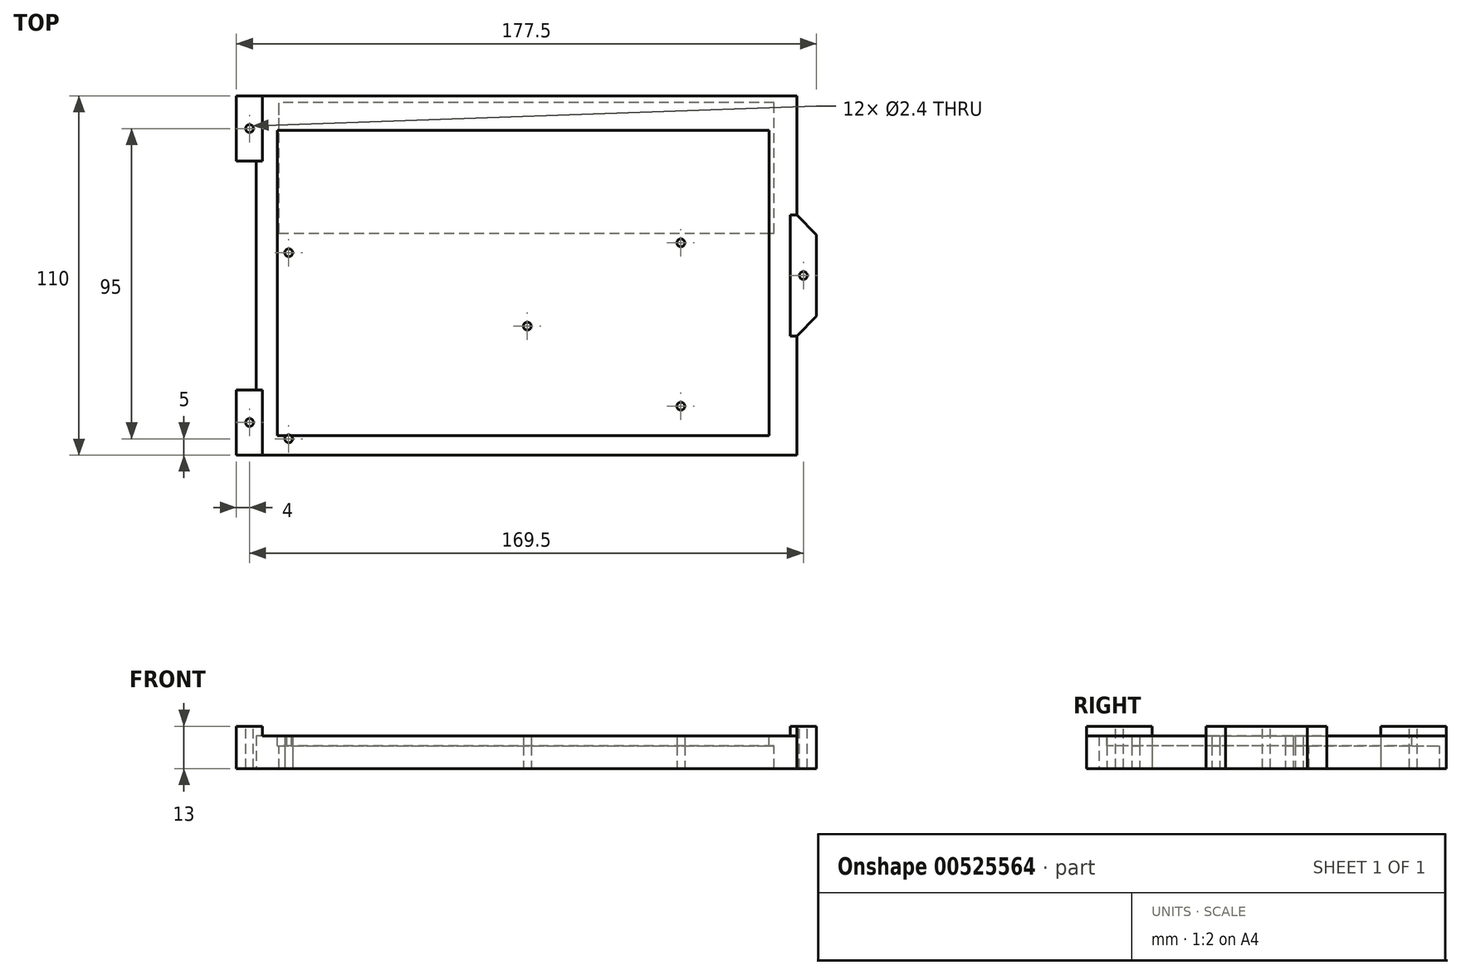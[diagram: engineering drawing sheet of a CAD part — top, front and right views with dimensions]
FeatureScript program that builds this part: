
annotation { "Feature Type Name" : "Feature", "Feature Type Description" : "" }
export const myFeature = defineFeature(function(context is Context, id is Id, definition is map)
    precondition{}
    {
        {
            var Q0;
            Q0=qCreatedBy(makeId("Top.planeOp"),FACE);
            var sketch = newSketch(context, id + "F0", { "sketchPlane" : qUnion([Q0])});
            skLineSegment(sketch, "E0.bottom", {"start": v(80.75, -53) * mm, "end": v(-80.75, -53) * mm});
            skLineSegment(sketch, "E0.top", {"start": v(80.75, 53) * mm, "end": v(-80.75, 53) * mm});
            skLineSegment(sketch, "E0.left", {"start": v(80.75, -53) * mm, "end": v(80.75, 53) * mm});
            skLineSegment(sketch, "E0.right", {"start": v(-80.75, -53) * mm, "end": v(-80.75, 53) * mm});
            skPoint(sketch, "E0.middle", {"position": v(0, 0) * mm});
            skLineSegment(sketch, "E1.bottom", {"start": v(82.75, -55) * mm, "end": v(-82.75, -55) * mm});
            skLineSegment(sketch, "E1.top", {"start": v(82.75, 55) * mm, "end": v(-82.75, 55) * mm});
            skLineSegment(sketch, "E1.left", {"start": v(82.75, -55) * mm, "end": v(82.75, 55) * mm});
            skLineSegment(sketch, "E1.right", {"start": v(-82.75, -55) * mm, "end": v(-82.75, 55) * mm});
            skLineSegment(sketch, "E2.bottom", {"start": v(-82.75, 55) * mm, "end": v(-88.75, 55) * mm});
            skLineSegment(sketch, "E2.top", {"start": v(-82.75, 35) * mm, "end": v(-88.75, 35) * mm});
            skLineSegment(sketch, "E2.left", {"start": v(-82.75, 55) * mm, "end": v(-82.75, 35) * mm});
            skLineSegment(sketch, "E2.right", {"start": v(-88.75, 55) * mm, "end": v(-88.75, 35) * mm});
            skLineSegment(sketch, "E3.bottom", {"start": v(-82.75, -55) * mm, "end": v(-88.75, -55) * mm});
            skLineSegment(sketch, "E3.top", {"start": v(-82.75, -35) * mm, "end": v(-88.75, -35) * mm});
            skLineSegment(sketch, "E3.left", {"start": v(-82.75, -55) * mm, "end": v(-82.75, -35) * mm});
            skLineSegment(sketch, "E3.right", {"start": v(-88.75, -55) * mm, "end": v(-88.75, -35) * mm});
            skLineSegment(sketch, "E4", {"start": v(88.75, 12.5) * mm, "end": v(88.75, -12.5) * mm});
            skLineSegment(sketch, "E5", {"start": v(88.75, -12.5) * mm, "end": v(82.75, -18.5) * mm});
            skLineSegment(sketch, "E6", {"start": v(88.75, 12.5) * mm, "end": v(82.75, 18.5) * mm});
            skSolve(sketch);
        }
        {
            var Q0;
            Q0 = qSketchRegion(id + "F0", true);
            extrude(context, id + "F1", {"entities" : qUnion([Q0]), "depth" : 10 * mm, "offsetDistance" : 25 * mm});
        }
        {
            var Q0;
            Q0=makeQuery(id+"F1.opExtrude","CAP_FACE",FACE,{"disambiguationData":[OSD([sQuery(id+"F0.wireOp",EDGE,"E0.bottom"),sQuery(id+"F0.wireOp",EDGE,"E0.top"),sQuery(id+"F0.wireOp",EDGE,"E0.left"),sQuery(id+"F0.wireOp",EDGE,"E0.right"),sQuery(id+"F0.wireOp",EDGE,"E1.bottom"),sQuery(id+"F0.wireOp",EDGE,"E1.top"),sQuery(id+"F0.wireOp",EDGE,"E1.left"),sQuery(id+"F0.wireOp",EDGE,"E1.right")])],"isStart":true});
            var sketch = newSketch(context, id + "F2", { "sketchPlane" : qUnion([Q0])});
            skLineSegment(sketch, "E7.bottom", {"start": v(-80.75, -53) * mm, "end": v(80.75, -53) * mm});
            skLineSegment(sketch, "E7.top", {"start": v(-80.75, 53) * mm, "end": v(80.75, 53) * mm});
            skLineSegment(sketch, "E7.left", {"start": v(-80.75, -53) * mm, "end": v(-80.75, 53) * mm});
            skLineSegment(sketch, "E7.right", {"start": v(80.75, -53) * mm, "end": v(80.75, 53) * mm});
            skSolve(sketch);
        }
        {
            var Q0;
            Q0 = qSketchRegion(id + "F2", true);
            extrude(context, id + "F3", {"entities" : qUnion([Q0]), "operationType" : NewBodyOperationType.ADD, "oppositeDirection" : true, "depth" : 7 * mm, "offsetDistance" : 25 * mm});
        }
        {
            var Q0;
            Q0=makeQuery(id+"F3.opExtrude","CAP_FACE",FACE,{"disambiguationData":[OSD([sQuery(id+"F2.wireOp",EDGE,"E7.bottom"),sQuery(id+"F2.wireOp",EDGE,"E7.top"),sQuery(id+"F2.wireOp",EDGE,"E7.left"),sQuery(id+"F2.wireOp",EDGE,"E7.right"),sQuery(id+"F2.wireOp",EDGE,"8f1VSSML-MHzT-LLwI-i7uZ-ldg2s0lFS6Cz.bottom"),sQuery(id+"F2.wireOp",EDGE,"8f1VSSML-MHzT-LLwI-i7uZ-ldg2s0lFS6Cz.top"),sQuery(id+"F2.wireOp",EDGE,"8f1VSSML-MHzT-LLwI-i7uZ-ldg2s0lFS6Cz.left"),sQuery(id+"F2.wireOp",EDGE,"8f1VSSML-MHzT-LLwI-i7uZ-ldg2s0lFS6Cz.right")])],"isStart":false});
            var sketch = newSketch(context, id + "F4", { "sketchPlane" : qUnion([Q0])});
            skLineSegment(sketch, "E8.bottom", {"start": v(-75.75, 13) * mm, "end": v(75.75, 13) * mm});
            skLineSegment(sketch, "E8.top", {"start": v(-75.75, 53) * mm, "end": v(75.75, 53) * mm});
            skLineSegment(sketch, "E8.left", {"start": v(-75.75, 13) * mm, "end": v(-75.75, 53) * mm});
            skLineSegment(sketch, "E8.right", {"start": v(75.75, 13) * mm, "end": v(75.75, 53) * mm});
            skSolve(sketch);
        }
        {
            var Q0;
            Q0 = qSketchRegion(id + "F4", true);
            extrude(context, id + "F5", {"entities" : qUnion([Q0]), "operationType" : NewBodyOperationType.REMOVE, "oppositeDirection" : true, "depth" : 25 * mm, "offsetDistance" : 25 * mm});
        }
        {
            var Q0;
            Q0=makeQuery(id+"F3.opExtrude","CAP_FACE",FACE,{"disambiguationData":[OSD([sQuery(id+"F2.wireOp",EDGE,"E7.bottom"),sQuery(id+"F2.wireOp",EDGE,"E7.top"),sQuery(id+"F2.wireOp",EDGE,"E7.left"),sQuery(id+"F2.wireOp",EDGE,"E7.right"),sQuery(id+"F2.wireOp",EDGE,"8f1VSSML-MHzT-LLwI-i7uZ-ldg2s0lFS6Cz.bottom"),sQuery(id+"F2.wireOp",EDGE,"8f1VSSML-MHzT-LLwI-i7uZ-ldg2s0lFS6Cz.top"),sQuery(id+"F2.wireOp",EDGE,"8f1VSSML-MHzT-LLwI-i7uZ-ldg2s0lFS6Cz.left"),sQuery(id+"F2.wireOp",EDGE,"8f1VSSML-MHzT-LLwI-i7uZ-ldg2s0lFS6Cz.right")])],"isStart":false});
            var sketch = newSketch(context, id + "F6", { "sketchPlane" : qUnion([Q0])});
            skLineSegment(sketch, "E9.bottom", {"start": v(-76.25, 44.5) * mm, "end": v(74.25, 44.5) * mm});
            skLineSegment(sketch, "E9.top", {"start": v(-76.25, -49) * mm, "end": v(74.25, -49) * mm});
            skLineSegment(sketch, "E9.left", {"start": v(-76.25, 44.5) * mm, "end": v(-76.25, -49) * mm});
            skLineSegment(sketch, "E9.right", {"start": v(74.25, 44.5) * mm, "end": v(74.25, -49) * mm});
            skLineSegment(sketch, "E10.bottom", {"start": v(80.75, -53) * mm, "end": v(-80.75, -53) * mm});
            skLineSegment(sketch, "E10.top", {"start": v(80.75, 53) * mm, "end": v(-80.75, 53) * mm});
            skLineSegment(sketch, "E10.left", {"start": v(80.75, -53) * mm, "end": v(80.75, 53) * mm});
            skLineSegment(sketch, "E10.right", {"start": v(-80.75, -53) * mm, "end": v(-80.75, 53) * mm});
            skPoint(sketch, "E10.middle", {"position": v(0, 0) * mm});
            skSolve(sketch);
        }
        {
            var Q0;
            Q0 = qSketchRegion(id + "F6", true);
            extrude(context, id + "F7", {"entities" : qUnion([Q0]), "depth" : 3 * mm, "offsetDistance" : 25 * mm});
        }
        {
            var Q0;
            Q0=makeQuery(id+"F7.opExtrude","CAP_FACE",FACE,{"disambiguationData":[OSD([sQuery(id+"F6.wireOp",EDGE,"E9.bottom"),sQuery(id+"F6.wireOp",EDGE,"E9.top"),sQuery(id+"F6.wireOp",EDGE,"E9.left"),sQuery(id+"F6.wireOp",EDGE,"E9.right"),sQuery(id+"F6.wireOp",EDGE,"E10.bottom"),sQuery(id+"F6.wireOp",EDGE,"E10.top"),sQuery(id+"F6.wireOp",EDGE,"E10.left"),sQuery(id+"F6.wireOp",EDGE,"E10.right")])],"isStart":false});
            var sketch = newSketch(context, id + "F8", { "sketchPlane" : qUnion([Q0])});
            skLineSegment(sketch, "E11.bottom", {"start": v(-76.25, 44.5) * mm, "end": v(74.25, 44.5) * mm});
            skLineSegment(sketch, "E11.top", {"start": v(-76.25, -49) * mm, "end": v(74.25, -49) * mm});
            skLineSegment(sketch, "E11.left", {"start": v(-76.25, 44.5) * mm, "end": v(-76.25, -49) * mm});
            skLineSegment(sketch, "E11.right", {"start": v(74.25, 44.5) * mm, "end": v(74.25, -49) * mm});
            skSolve(sketch);
        }
        {
            var Q0;
            Q0 = qSketchRegion(id + "F8", true);
            extrude(context, id + "F9", {"entities" : qUnion([Q0]), "oppositeDirection" : true, "depth" : 3 * mm, "offsetDistance" : 25 * mm});
        }
        {
            var Q0;
            Q0=makeQuery(id+"F1.opExtrude","CAP_FACE",FACE,{"disambiguationData":[OSD([sQuery(id+"F0.wireOp",EDGE,"E0.bottom"),sQuery(id+"F0.wireOp",EDGE,"E0.top"),sQuery(id+"F0.wireOp",EDGE,"E0.left"),sQuery(id+"F0.wireOp",EDGE,"E0.right"),sQuery(id+"F0.wireOp",EDGE,"E1.bottom"),sQuery(id+"F0.wireOp",EDGE,"E1.top"),sQuery(id+"F0.wireOp",EDGE,"E1.left"),sQuery(id+"F0.wireOp",EDGE,"E1.right"),sQuery(id+"F0.wireOp",EDGE,"oeJhyEZn-X8Gv-NV8l-QlPN-WZpYdueP7FPk"),sQuery(id+"F0.wireOp",EDGE,"t7SqtOqI-6Vzl-XjQY-wyfs-TwdQ3bBUR3kO"),sQuery(id+"F0.wireOp",EDGE,"vmnc4yMv-dyLv-snxY-bUmN-Fs4h2lBnpgQ6"),sQuery(id+"F0.wireOp",EDGE,"WREx9Z0f-3UMY-QVX8-n1f2-vJOwg17c67VE"),sQuery(id+"F0.wireOp",EDGE,"yMH2aO68-bz5t-1Wbc-TLPJ-5kFjG3eKHg8o"),sQuery(id+"F0.wireOp",EDGE,"54VUKrqb-FPuZ-dD4I-ghqg-f8SScJDziYSC"),sQuery(id+"F0.wireOp",EDGE,"E75IO5ob-jJ6u-f5Z0-xtuM-XlgKxU9iRORH"),sQuery(id+"F0.wireOp",EDGE,"YjTzF3YZ-eKyh-XalN-2II3-zwrFt94DyLal"),sQuery(id+"F0.wireOp",EDGE,"wFoRUqGF-yFK8-S5Ye-rNy3-0qYocYTKUupg")])],"isStart":false});
            var sketch = newSketch(context, id + "F10", { "sketchPlane" : qUnion([Q0])});
            skLineSegment(sketch, "E12.bottom", {"start": v(-88.75, 55) * mm, "end": v(-80.75, 55) * mm});
            skLineSegment(sketch, "E12.top", {"start": v(-88.75, 35) * mm, "end": v(-80.75, 35) * mm});
            skLineSegment(sketch, "E12.left", {"start": v(-88.75, 55) * mm, "end": v(-88.75, 35) * mm});
            skLineSegment(sketch, "E12.right", {"start": v(-80.75, 55) * mm, "end": v(-80.75, 35) * mm});
            skLineSegment(sketch, "E13.bottom", {"start": v(-88.75, -55) * mm, "end": v(-80.75, -55) * mm});
            skLineSegment(sketch, "E13.top", {"start": v(-88.75, -35) * mm, "end": v(-80.75, -35) * mm});
            skLineSegment(sketch, "E13.left", {"start": v(-88.75, -55) * mm, "end": v(-88.75, -35) * mm});
            skLineSegment(sketch, "E13.right", {"start": v(-80.75, -55) * mm, "end": v(-80.75, -35) * mm});
            skLineSegment(sketch, "E14", {"start": v(82.75, 18.5) * mm, "end": v(88.75, 12.5) * mm});
            skLineSegment(sketch, "E15", {"start": v(88.75, 12.5) * mm, "end": v(88.75, -12.5) * mm});
            skLineSegment(sketch, "E16", {"start": v(88.75, -12.5) * mm, "end": v(82.75, -18.5) * mm});
            skLineSegment(sketch, "E17", {"start": v(82.75, -18.5) * mm, "end": v(80.75, -18.5) * mm});
            skLineSegment(sketch, "E18", {"start": v(80.75, -18.5) * mm, "end": v(80.75, 18.5) * mm});
            skLineSegment(sketch, "E19", {"start": v(80.75, 18.5) * mm, "end": v(82.75, 18.5) * mm});
            skSolve(sketch);
        }
        {
            var Q0;
            Q0 = qSketchRegion(id + "F10", true);
            extrude(context, id + "F11", {"entities" : qUnion([Q0]), "operationType" : NewBodyOperationType.ADD, "depth" : 3 * mm, "offsetDistance" : 25 * mm});
        }
        {
            var Q0;
            Q0=makeQuery(id+"F11.opExtrude","CAP_FACE",FACE,{"disambiguationData":[OSD([sQuery(id+"F10.wireOp",EDGE,"E12.bottom"),sQuery(id+"F10.wireOp",EDGE,"E12.top"),sQuery(id+"F10.wireOp",EDGE,"E12.left"),sQuery(id+"F10.wireOp",EDGE,"E12.right")])],"isStart":false});
            var sketch = newSketch(context, id + "F12", { "sketchPlane" : qUnion([Q0])});
            skCircle(sketch, "E20", {"center": v(-84.75, 45) * mm, "radius": 1.2 * mm});
            skCircle(sketch, "E21", {"center": v(84.75, 0) * mm, "radius": 1.2 * mm});
            skCircle(sketch, "E22", {"center": v(-84.75, -45) * mm, "radius": 1.2 * mm});
            skSolve(sketch);
        }
        {
            var Q0;
            Q0 = qSketchRegion(id + "F12", true);
            extrude(context, id + "F13", {"entities" : qUnion([Q0]), "operationType" : NewBodyOperationType.REMOVE, "oppositeDirection" : true, "depth" : 25 * mm, "offsetDistance" : 25 * mm});
        }
        {
            var Q0;
            Q0=makeQuery(id+"F3.boolean.opBoolean","MERGE",FACE,{"derivedFrom":[makeQuery(id+"F1.opExtrude","CAP_FACE",FACE,{"disambiguationData":[OSD([sQuery(id+"F0.wireOp",EDGE,"E0.bottom"),sQuery(id+"F0.wireOp",EDGE,"E0.top"),sQuery(id+"F0.wireOp",EDGE,"E0.left"),sQuery(id+"F0.wireOp",EDGE,"E0.right"),sQuery(id+"F0.wireOp",EDGE,"E1.bottom"),sQuery(id+"F0.wireOp",EDGE,"E1.top"),sQuery(id+"F0.wireOp",EDGE,"E1.left"),sQuery(id+"F0.wireOp",EDGE,"E1.right"),sQuery(id+"F0.wireOp",EDGE,"oeJhyEZn-X8Gv-NV8l-QlPN-WZpYdueP7FPk"),sQuery(id+"F0.wireOp",EDGE,"t7SqtOqI-6Vzl-XjQY-wyfs-TwdQ3bBUR3kO"),sQuery(id+"F0.wireOp",EDGE,"vmnc4yMv-dyLv-snxY-bUmN-Fs4h2lBnpgQ6"),sQuery(id+"F0.wireOp",EDGE,"WREx9Z0f-3UMY-QVX8-n1f2-vJOwg17c67VE"),sQuery(id+"F0.wireOp",EDGE,"YjTzF3YZ-eKyh-XalN-2II3-zwrFt94DyLal"),sQuery(id+"F0.wireOp",EDGE,"QCJemlNQ-ldeu-oOYi-F3ud-SHuWPldmH4UB"),sQuery(id+"F0.wireOp",EDGE,"Fbhjdizr-ISwi-HiPS-y7Ga-ycMwwiKzc9SH"),sQuery(id+"F0.wireOp",EDGE,"5hEYKqD0-A6P0-qPGR-DnJO-wmdxlUmYokK9"),sQuery(id+"F0.wireOp",EDGE,"hOOjNGGI-lq84-WY0j-wMxB-aX63JgCsEcVZ")])],"isStart":true}),makeQuery(id+"F3.opExtrude","CAP_FACE",FACE,{"disambiguationData":[OSD([sQuery(id+"F2.wireOp",EDGE,"E7.bottom"),sQuery(id+"F2.wireOp",EDGE,"E7.top"),sQuery(id+"F2.wireOp",EDGE,"E7.left"),sQuery(id+"F2.wireOp",EDGE,"E7.right")])],"isStart":true})]});
            var sketch = newSketch(context, id + "F14", { "sketchPlane" : qUnion([Q0])});
            skCircle(sketch, "E23", {"center": v(-72.75, 50) * mm, "radius": 1.2 * mm});
            skCircle(sketch, "E24", {"center": v(-72.75, -7) * mm, "radius": 1.2 * mm});
            skCircle(sketch, "E25", {"center": v(47.25, 40) * mm, "radius": 1.2 * mm});
            skCircle(sketch, "E26", {"center": v(47.25, -10) * mm, "radius": 1.2 * mm});
            skLineSegment(sketch, "E27.bottom", {"start": v(42.25, -25) * mm, "end": v(52.25, -25) * mm, "construction": true});
            skLineSegment(sketch, "E27.top", {"start": v(42.25, 55) * mm, "end": v(52.25, 55) * mm, "construction": true});
            skLineSegment(sketch, "E27.left", {"start": v(42.25, -25) * mm, "end": v(42.25, 55) * mm, "construction": true});
            skLineSegment(sketch, "E27.right", {"start": v(52.25, -25) * mm, "end": v(52.25, 55) * mm, "construction": true});
            skPoint(sketch, "E27.middle", {"position": v(47.25, 15) * mm});
            skCircle(sketch, "E28", {"center": v(0.25, 15.5) * mm, "radius": 1.2 * mm});
            skSolve(sketch);
        }
        {
            var Q0;
            Q0 = qSketchRegion(id + "F14", true);
            extrude(context, id + "F15", {"entities" : qUnion([Q0]), "operationType" : NewBodyOperationType.REMOVE, "oppositeDirection" : true, "depth" : 25 * mm, "offsetDistance" : 25 * mm});
        }
    });
